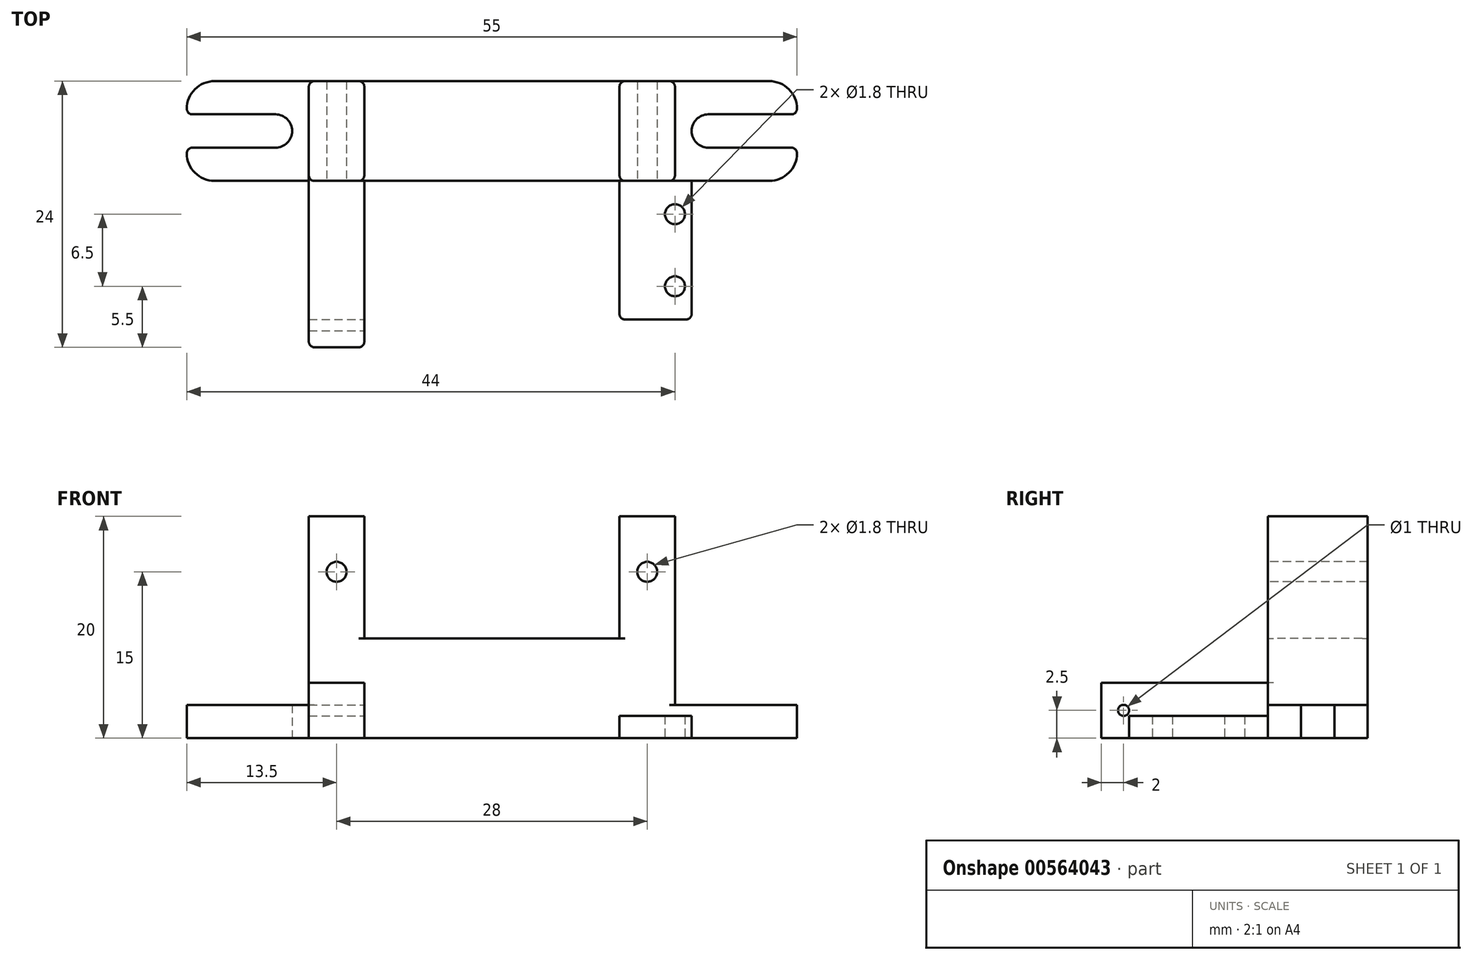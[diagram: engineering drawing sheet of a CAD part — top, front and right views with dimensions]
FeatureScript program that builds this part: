
annotation { "Feature Type Name" : "Feature", "Feature Type Description" : "" }
export const myFeature = defineFeature(function(context is Context, id is Id, definition is map)
    precondition{}
    {
        {
            var Q0;
            Q0=qCreatedBy(makeId("Top.planeOp"),FACE);
            var sketch = newSketch(context, id + "F0", { "sketchPlane" : qUnion([Q0])});
            skLineSegment(sketch, "E0.bottom", {"start": v(-25, 4.5) * mm, "end": v(25, 4.5) * mm});
            skLineSegment(sketch, "E0.top", {"start": v(-25, -4.5) * mm, "end": v(25, -4.5) * mm});
            skLineSegment(sketch, "E0.left", {"start": v(-27.5, 2) * mm, "end": v(-27.5, 1.5) * mm});
            skLineSegment(sketch, "E0.right", {"start": v(27.5, 2) * mm, "end": v(27.5, 1.5) * mm});
            skPoint(sketch, "E0.middle", {"position": v(0, 0) * mm});
            skLineSegment(sketch, "E1", {"start": v(-16.5, 4.5) * mm, "end": v(-16.5, -4.5) * mm});
            skLineSegment(sketch, "E2", {"start": v(-11.5, 4.5) * mm, "end": v(-11.5, -4.5) * mm});
            skLineSegment(sketch, "E3", {"start": v(0, 4.5) * mm, "end": v(0, -4.5) * mm, "construction": true});
            skArc(sketch, "E4", {"start": v(-19.5, -1.5) * mm, "mid": v(-18, 0) * mm, "end": v(-19.5, 1.5) * mm});
            skPoint(sketch, "E5.visualSharp", {"position": v(-27.5, 4.5) * mm});
            skArc(sketch, "E5.filletArc", {"start": v(-25, 4.5) * mm, "mid": v(-26.77, 3.77) * mm, "end": v(-27.5, 2) * mm});
            skPoint(sketch, "E6.visualSharp", {"position": v(-27.5, -4.5) * mm});
            skArc(sketch, "E6.filletArc", {"start": v(-27.5, -2) * mm, "mid": v(-26.77, -3.77) * mm, "end": v(-25, -4.5) * mm});
            skPoint(sketch, "E7.visualSharp", {"position": v(27.5, 4.5) * mm});
            skArc(sketch, "E7.filletArc", {"start": v(27.5, 2) * mm, "mid": v(26.77, 3.77) * mm, "end": v(25, 4.5) * mm});
            skPoint(sketch, "E8.visualSharp", {"position": v(27.5, -4.5) * mm});
            skArc(sketch, "E8.filletArc", {"start": v(25, -4.5) * mm, "mid": v(26.77, -3.77) * mm, "end": v(27.5, -2) * mm});
            skLineSegment(sketch, "E9.MirrorCS", {"start": v(11.5, 4.5) * mm, "end": v(11.5, -4.5) * mm});
            skLineSegment(sketch, "E10.MirrorCS", {"start": v(16.5, 4.5) * mm, "end": v(16.5, -4.5) * mm});
            skArc(sketch, "E11.MirrorCS", {"start": v(19.5, -1.5) * mm, "mid": v(18, 0) * mm, "end": v(19.5, 1.5) * mm});
            skLineSegment(sketch, "E12.bottom", {"start": v(-11.5, 4.5) * mm, "end": v(-16.5, 4.5) * mm});
            skLineSegment(sketch, "E12.top", {"start": v(-11.5, -19.5) * mm, "end": v(-16.5, -19.5) * mm});
            skLineSegment(sketch, "E12.left", {"start": v(-11.5, 4.5) * mm, "end": v(-11.5, -19.5) * mm});
            skLineSegment(sketch, "E12.right", {"start": v(-16.5, 4.5) * mm, "end": v(-16.5, -19.5) * mm});
            skLineSegment(sketch, "E13", {"start": v(-19.5, 1.5) * mm, "end": v(-27.5, 1.5) * mm});
            skLineSegment(sketch, "E14", {"start": v(-19.5, -1.5) * mm, "end": v(-27.5, -1.5) * mm});
            skLineSegment(sketch, "E15.trimOffspring", {"start": v(-27.5, -1.5) * mm, "end": v(-27.5, -2) * mm});
            skLineSegment(sketch, "E16", {"start": v(19.5, -1.5) * mm, "end": v(27.5, -1.5) * mm});
            skLineSegment(sketch, "E17", {"start": v(19.5, 1.5) * mm, "end": v(27.5, 1.5) * mm});
            skLineSegment(sketch, "E18.trimOffspring", {"start": v(27.5, -1.5) * mm, "end": v(27.5, -2) * mm});
            skSolve(sketch);
        }
        {
            var Q0;
            Q0=makeQuery(id+"F0.imprint","IMPRINT",FACE,{"disambiguationData":[TD([[makeQuery(id+"F0.imprint","IMPRINT",EDGE,{"derivedFrom":sQuery(id+"F0.wireOp",EDGE,"E0.left")}),1.0]])]});
            var Q1;
            Q1=makeQuery(id+"F0.imprint","IMPRINT",FACE,{"disambiguationData":[TD([[makeQuery(id+"F0.imprint","IMPRINT",EDGE,{"derivedFrom":sQuery(id+"F0.wireOp",EDGE,"E0.right")}),-1.0]])]});
            var Q2;
            {var subQ2=sQuery(id+"F0.wireOp",EDGE,"E1");Q2=makeQuery(id+"F0.imprint","IMPRINT",FACE,{"disambiguationData":[TD([[makeQuery(id+"F0.imprint","IMPRINT",EDGE,{"derivedFrom":subQ2}),1.0]])]});}
            var Q3;
            {var subQ0=sQuery(id+"F0.wireOp",EDGE,"E9.MirrorCS");Q3=makeQuery(id+"F0.imprint","IMPRINT",FACE,{"disambiguationData":[TD([[makeQuery(id+"F0.imprint","IMPRINT",EDGE,{"derivedFrom":subQ0}),1.0]])]});}
            var Q4;
            {var subQ0=sQuery(id+"F0.wireOp",EDGE,"E2");Q4=makeQuery(id+"F0.imprint","IMPRINT",FACE,{"disambiguationData":[TD([[makeQuery(id+"F0.imprint","IMPRINT",EDGE,{"derivedFrom":subQ0}),1.0]])]});}
            extrude(context, id + "F1", {"entities" : qUnion([Q0, Q1, Q2, Q3, Q4]), "depth" : 3 * mm, "offsetDistance" : 25 * mm});
        }
        {
            var Q0;
            {var subQ0=sQuery(id+"F0.wireOp",EDGE,"E9.MirrorCS");Q0=makeQuery(id+"F0.imprint","IMPRINT",FACE,{"disambiguationData":[TD([[makeQuery(id+"F0.imprint","IMPRINT",EDGE,{"derivedFrom":subQ0}),1.0]])]});}
            var Q1;
            {var subQ2=sQuery(id+"F0.wireOp",EDGE,"E1");Q1=makeQuery(id+"F0.imprint","IMPRINT",FACE,{"disambiguationData":[TD([[makeQuery(id+"F0.imprint","IMPRINT",EDGE,{"derivedFrom":subQ2}),1.0]])]});}
            extrude(context, id + "F2", {"entities" : qUnion([Q0, Q1]), "operationType" : NewBodyOperationType.ADD, "depth" : 20 * mm, "offsetDistance" : 25 * mm});
        }
        {
            var Q0;
            {var subQ0=sQuery(id+"F0.wireOp",EDGE,"E2");Q0=makeQuery(id+"F0.imprint","IMPRINT",FACE,{"disambiguationData":[TD([[makeQuery(id+"F0.imprint","IMPRINT",EDGE,{"derivedFrom":subQ0}),1.0]])]});}
            extrude(context, id + "F3", {"entities" : qUnion([Q0]), "operationType" : NewBodyOperationType.ADD, "depth" : (20 - 11) * mm, "offsetDistance" : 25 * mm});
        }
        {
            var Q0;
            Q0=makeQuery(id+"F0.imprint","IMPRINT",FACE,{"disambiguationData":[TD([[makeQuery(id+"F0.imprint","IMPRINT",EDGE,{"derivedFrom":sQuery(id+"F0.wireOp",EDGE,"E12.top")}),-1.0]])]});
            extrude(context, id + "F4", {"entities" : qUnion([Q0]), "operationType" : NewBodyOperationType.ADD, "depth" : 5 * mm, "offsetDistance" : 25 * mm});
        }
        {
            var Q0;
            Q0=makeQuery(id+"F4.opExtrude","SWEPT_FACE",FACE,{"disambiguationData":[OSD([sQuery(id+"F0.wireOp",EDGE,"E12.left")])]});
            var sketch = newSketch(context, id + "F5", { "sketchPlane" : qUnion([Q0])});
            skLineSegment(sketch, "E19", {"start": v(-19.5, 2.5) * mm, "end": v(-4.5, 2.5) * mm, "construction": true});
            skCircle(sketch, "E20", {"center": v(-17.5, 2.5) * mm, "radius": 0.5 * mm});
            skSolve(sketch);
        }
        {
            var Q0;
            Q0 = qSketchRegion(id + "F5", true);
            extrude(context, id + "F6", {"entities" : qUnion([Q0]), "operationType" : NewBodyOperationType.REMOVE, "oppositeDirection" : true, "depth" : 25 * mm, "offsetDistance" : 25 * mm});
        }
        {
            var Q0;
            Q0=qCreatedBy(makeId("Top.planeOp"),FACE);
            var sketch = newSketch(context, id + "F7", { "sketchPlane" : qUnion([Q0])});
            skLineSegment(sketch, "E21.bottom", {"start": v(11.5, -4.5) * mm, "end": v(18, -4.5) * mm});
            skLineSegment(sketch, "E21.top", {"start": v(11.5, -17) * mm, "end": v(18, -17) * mm});
            skLineSegment(sketch, "E21.left", {"start": v(11.5, -4.5) * mm, "end": v(11.5, -17) * mm});
            skLineSegment(sketch, "E21.right", {"start": v(18, -4.5) * mm, "end": v(18, -17) * mm});
            skLineSegment(sketch, "E22", {"start": v(16.5, -4.5) * mm, "end": v(16.5, -17) * mm, "construction": true});
            skCircle(sketch, "E23", {"center": v(16.5, -7.5) * mm, "radius": 0.9 * mm});
            skCircle(sketch, "E24", {"center": v(16.5, -14) * mm, "radius": 0.9 * mm});
            skSolve(sketch);
        }
        {
            var Q0;
            Q0=makeQuery(id+"F7.imprint","IMPRINT",FACE,{"disambiguationData":[TD([[makeQuery(id+"F7.imprint","IMPRINT",EDGE,{"derivedFrom":sQuery(id+"F7.wireOp",EDGE,"E21.bottom")}),-1.0]])]});
            extrude(context, id + "F8", {"entities" : qUnion([Q0]), "operationType" : NewBodyOperationType.ADD, "depth" : 2 * mm, "offsetDistance" : 25 * mm});
        }
        {
            var Q0;
            {var subQ0=sQuery(id+"F0.wireOp",EDGE,"E10.MirrorCS");var subQ2=sQuery(id+"F0.wireOp",EDGE,"E2");var subQ3=sQuery(id+"F0.wireOp",EDGE,"E0.top");var subQ10=sQuery(id+"F0.wireOp",EDGE,"E8.filletArc");var subQ21=sQuery(id+"F0.wireOp",EDGE,"E12.left");Q0=makeQuery(id+"F4.boolean.opBoolean","SPLIT",FACE,{"disambiguationData":[TD([makeQuery(id+"F1.opExtrude","SWEPT_FACE",FACE,{"disambiguationData":[OSD([subQ10])]})])],"derivedFrom":makeQuery(id+"F3.boolean.opBoolean","MERGE",FACE,{"derivedFrom":[makeQuery(id+"F2.boolean.opBoolean","MERGE",FACE,{"derivedFrom":[makeQuery(id+"F1.opExtrude","SWEPT_FACE",FACE,{"disambiguationData":[OSD([subQ3])]}),makeQuery(id+"F2.opExtrude","SWEPT_FACE",FACE,{"disambiguationData":[OSD([subQ3]),TDD([makeQuery(id+"F0.imprint","IMPRINT",EDGE,{"disambiguationData":[TD([[makeQuery(id+"F0.imprint","INTERSECT",VERTEX,{"derivedFrom":[subQ3,subQ2,subQ21]}),1.0]])],"derivedFrom":subQ3})])]}),makeQuery(id+"F2.opExtrude","SWEPT_FACE",FACE,{"disambiguationData":[OSD([subQ3]),TDD([makeQuery(id+"F0.imprint","IMPRINT",EDGE,{"disambiguationData":[TD([[makeQuery(id+"F0.imprint","INTERSECT",VERTEX,{"derivedFrom":[subQ3,subQ0]}),1.0]])],"derivedFrom":subQ3})])]})]}),makeQuery(id+"F3.opExtrude","SWEPT_FACE",FACE,{"disambiguationData":[OSD([subQ3])]})]})});}
            var sketch = newSketch(context, id + "F9", { "sketchPlane" : qUnion([Q0])});
            skLineSegment(sketch, "E25", {"start": v(-14, 20) * mm, "end": v(-14, 5) * mm, "construction": true});
            skLineSegment(sketch, "E26", {"start": v(14, 20) * mm, "end": v(14, 2) * mm, "construction": true});
            skLineSegment(sketch, "E27", {"start": v(-16.5, 15) * mm, "end": v(16.5, 15) * mm, "construction": true});
            skCircle(sketch, "E28", {"center": v(-14, 15) * mm, "radius": 0.9 * mm});
            skCircle(sketch, "E29", {"center": v(14, 15) * mm, "radius": 0.9 * mm});
            skSolve(sketch);
        }
        {
            var Q0;
            Q0 = qSketchRegion(id + "F9", true);
            extrude(context, id + "F10", {"entities" : qUnion([Q0]), "operationType" : NewBodyOperationType.REMOVE, "oppositeDirection" : true, "depth" : 25 * mm, "offsetDistance" : 25 * mm});
        }
        {
            var Q0;
            Q0=makeQuery(id+"F8.opExtrude","SWEPT_EDGE",EDGE,{"disambiguationData":[OSD([sQuery(id+"F7.wireOp",EDGE,"E21.top"),sQuery(id+"F7.wireOp",EDGE,"E21.left")])]});
            var Q1;
            Q1=makeQuery(id+"F8.opExtrude","SWEPT_EDGE",EDGE,{"disambiguationData":[OSD([sQuery(id+"F7.wireOp",EDGE,"E21.top"),sQuery(id+"F7.wireOp",EDGE,"E21.right")])]});
            var Q2;
            Q2=makeQuery(id+"F4.opExtrude","SWEPT_EDGE",EDGE,{"disambiguationData":[OSD([sQuery(id+"F0.wireOp",EDGE,"E12.top"),sQuery(id+"F0.wireOp",EDGE,"E12.left")])]});
            var Q3;
            Q3=makeQuery(id+"F4.opExtrude","SWEPT_EDGE",EDGE,{"disambiguationData":[OSD([sQuery(id+"F0.wireOp",EDGE,"E12.top"),sQuery(id+"F0.wireOp",EDGE,"E12.right")])]});
            var Q4;
            Q4=makeQuery(id+"F2.opExtrude","SWEPT_EDGE",EDGE,{"disambiguationData":[OSD([sQuery(id+"F0.wireOp",EDGE,"E0.top"),sQuery(id+"F0.wireOp",EDGE,"E1"),sQuery(id+"F0.wireOp",EDGE,"E12.right")])]});
            var Q5;
            Q5=makeQuery(id+"F2.opExtrude","SWEPT_EDGE",EDGE,{"disambiguationData":[OSD([sQuery(id+"F0.wireOp",EDGE,"E0.top"),sQuery(id+"F0.wireOp",EDGE,"E9.MirrorCS")])]});
            var Q6;
            Q6=makeQuery(id+"F2.opExtrude","SWEPT_EDGE",EDGE,{"disambiguationData":[OSD([sQuery(id+"F0.wireOp",EDGE,"E0.top"),sQuery(id+"F0.wireOp",EDGE,"E2"),sQuery(id+"F0.wireOp",EDGE,"E12.left")])]});
            var Q7;
            Q7=makeQuery(id+"F2.opExtrude","SWEPT_EDGE",EDGE,{"disambiguationData":[OSD([sQuery(id+"F0.wireOp",EDGE,"E0.top"),sQuery(id+"F0.wireOp",EDGE,"E10.MirrorCS")])]});
            var Q8;
            Q8=makeQuery(id+"F2.opExtrude","SWEPT_EDGE",EDGE,{"disambiguationData":[OSD([sQuery(id+"F0.wireOp",EDGE,"E0.bottom"),sQuery(id+"F0.wireOp",EDGE,"E9.MirrorCS")])]});
            var Q9;
            Q9=makeQuery(id+"F2.opExtrude","SWEPT_EDGE",EDGE,{"disambiguationData":[OSD([sQuery(id+"F0.wireOp",EDGE,"E0.bottom"),sQuery(id+"F0.wireOp",EDGE,"E2")])]});
            var Q10;
            Q10=makeQuery(id+"F2.opExtrude","SWEPT_EDGE",EDGE,{"disambiguationData":[OSD([sQuery(id+"F0.wireOp",EDGE,"E0.bottom"),sQuery(id+"F0.wireOp",EDGE,"E1")])]});
            var Q11;
            Q11=makeQuery(id+"F2.opExtrude","SWEPT_EDGE",EDGE,{"disambiguationData":[OSD([sQuery(id+"F0.wireOp",EDGE,"E0.bottom"),sQuery(id+"F0.wireOp",EDGE,"E10.MirrorCS")])]});
            var Q12;
            Q12=makeQuery(id+"F1.opExtrude","SWEPT_EDGE",EDGE,{"disambiguationData":[OSD([sQuery(id+"F0.wireOp",EDGE,"E0.left"),sQuery(id+"F0.wireOp",EDGE,"E13")])]});
            var Q13;
            Q13=makeQuery(id+"F1.opExtrude","SWEPT_EDGE",EDGE,{"disambiguationData":[OSD([sQuery(id+"F0.wireOp",EDGE,"E14"),sQuery(id+"F0.wireOp",EDGE,"E15.trimOffspring")])]});
            var Q14;
            Q14=makeQuery(id+"F1.opExtrude","SWEPT_EDGE",EDGE,{"disambiguationData":[OSD([sQuery(id+"F0.wireOp",EDGE,"E0.right"),sQuery(id+"F0.wireOp",EDGE,"E17")])]});
            var Q15;
            Q15=makeQuery(id+"F1.opExtrude","SWEPT_EDGE",EDGE,{"disambiguationData":[OSD([sQuery(id+"F0.wireOp",EDGE,"E16"),sQuery(id+"F0.wireOp",EDGE,"E18.trimOffspring")])]});
            fillet(context, id + "F11", {"entities" : qUnion([Q0, Q1, Q2, Q3, Q4, Q5, Q6, Q7, Q8, Q9, Q10, Q11, Q12, Q13, Q14, Q15]), "tangentPropagation" : true, "radius" : 0.5 * mm, "defaultsChanged" : false, "vertexSettings" : [], "allowEdgeOverflow" : false});
        }
    });
